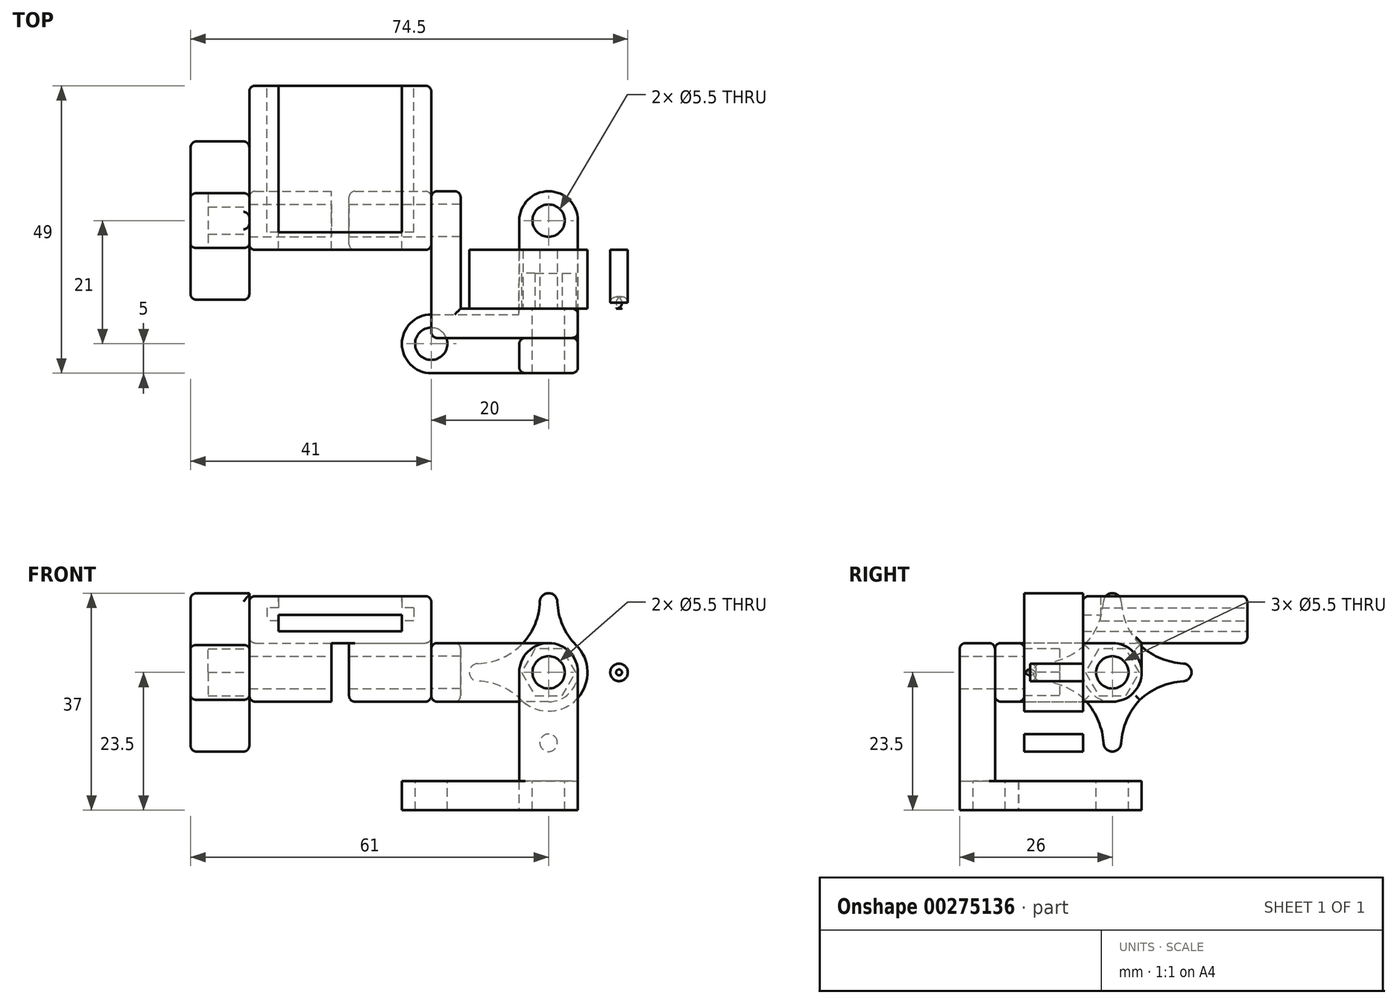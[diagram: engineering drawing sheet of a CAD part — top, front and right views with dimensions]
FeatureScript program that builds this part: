
annotation { "Feature Type Name" : "Feature", "Feature Type Description" : "" }
export const myFeature = defineFeature(function(context is Context, id is Id, definition is map)
    precondition{}
    {
        {
            var Q0;
            Q0=qCreatedBy(makeId("Top.planeOp"),FACE);
            var sketch = newSketch(context, id + "F0", { "sketchPlane" : qUnion([Q0])});
            skLineSegment(sketch, "E0.bottom", {"start": v(-15.5, 14) * mm, "end": v(15.5, 14) * mm});
            skLineSegment(sketch, "E0.top", {"start": v(-15.5, -14) * mm, "end": v(15.5, -14) * mm});
            skLineSegment(sketch, "E0.left", {"start": v(-15.5, 14) * mm, "end": v(-15.5, -14) * mm});
            skLineSegment(sketch, "E0.right", {"start": v(15.5, 14) * mm, "end": v(15.5, -14) * mm});
            skPoint(sketch, "E1", {"position": v(0, 14) * mm});
            skPoint(sketch, "E2", {"position": v(-15.5, 0) * mm});
            skSolve(sketch);
        }
        {
            var Q0;
            Q0=makeQuery(id+"F0.imprint","IMPRINT",FACE,{"disambiguationData":[TD([[makeQuery(id+"F0.imprint","IMPRINT",EDGE,{"derivedFrom":sQuery(id+"F0.wireOp",EDGE,"E0.bottom")}),-1.0]])]});
            extrude(context, id + "F1", {"entities" : qUnion([Q0]), "depth" : (4 + 4) * mm});
        }
        {
            var Q0;
            Q0=makeQuery(id+"F1.opExtrude","SWEPT_FACE",FACE,{"disambiguationData":[OSD([sQuery(id+"F0.wireOp",EDGE,"E0.bottom")])]});
            var sketch = newSketch(context, id + "F2", { "sketchPlane" : qUnion([Q0])});
            skLineSegment(sketch, "E3.bottom", {"start": v(-12.5, 6) * mm, "end": v(12.5, 6) * mm});
            skLineSegment(sketch, "E3.top", {"start": v(-12.5, 4.8) * mm, "end": v(12.5, 4.8) * mm});
            skLineSegment(sketch, "E3.left", {"start": v(-12.5, 6) * mm, "end": v(-12.5, 4.8) * mm});
            skLineSegment(sketch, "E3.right", {"start": v(12.5, 6) * mm, "end": v(12.5, 4.8) * mm});
            skLineSegment(sketch, "E4.bottom", {"start": v(-10.5, 8) * mm, "end": v(10.5, 8) * mm});
            skLineSegment(sketch, "E4.top", {"start": v(-10.5, 2) * mm, "end": v(10.5, 2) * mm});
            skLineSegment(sketch, "E4.left", {"start": v(-10.5, 8) * mm, "end": v(-10.5, 2) * mm});
            skLineSegment(sketch, "E4.right", {"start": v(10.5, 8) * mm, "end": v(10.5, 2) * mm});
            skSolve(sketch);
        }
        {
            var Q0;
            {var subQ5=sQuery(id+"F2.wireOp",EDGE,"E4.bottom");Q0=makeQuery(id+"F2.imprint","IMPRINT",FACE,{"disambiguationData":[TD([[makeQuery(id+"F2.imprint","IMPRINT",EDGE,{"derivedFrom":subQ5}),1.0]])]});}
            var Q1;
            {var subQ0=sQuery(id+"F2.wireOp",EDGE,"E4.left");var subQ1=sQuery(id+"F2.wireOp",EDGE,"E3.bottom");var subQ2=makeQuery(id+"F2.imprint","INTERSECT",VERTEX,{"derivedFrom":[subQ1,subQ0]});Q1=makeQuery(id+"F2.imprint","IMPRINT",FACE,{"disambiguationData":[TD([[makeQuery(id+"F2.imprint","IMPRINT",EDGE,{"disambiguationData":[TD([[subQ2,-1.0]])],"derivedFrom":subQ1}),-1.0]])]});}
            var Q2;
            {var subQ0=sQuery(id+"F2.wireOp",EDGE,"E3.left");Q2=makeQuery(id+"F2.imprint","IMPRINT",FACE,{"disambiguationData":[TD([[makeQuery(id+"F2.imprint","IMPRINT",EDGE,{"derivedFrom":subQ0}),1.0]])]});}
            var Q3;
            {var subQ5=sQuery(id+"F2.wireOp",EDGE,"E4.top");Q3=makeQuery(id+"F2.imprint","IMPRINT",FACE,{"disambiguationData":[TD([[makeQuery(id+"F2.imprint","IMPRINT",EDGE,{"derivedFrom":subQ5}),1.0]])]});}
            var Q4;
            {var subQ0=sQuery(id+"F2.wireOp",EDGE,"E3.right");Q4=makeQuery(id+"F2.imprint","IMPRINT",FACE,{"disambiguationData":[TD([[makeQuery(id+"F2.imprint","IMPRINT",EDGE,{"derivedFrom":subQ0}),-1.0]])]});}
            extrude(context, id + "F3", {"entities" : qUnion([Q0, Q1, Q2, Q3, Q4]), "operationType" : NewBodyOperationType.REMOVE, "oppositeDirection" : true, "depth" : 25 * mm});
        }
        {
            var Q0;
            Q0=makeQuery(id+"F3.boolean.opBoolean","COPY",FACE,{"derivedFrom":makeQuery(id+"F3.opExtrude","CAP_FACE",FACE,{"disambiguationData":[OSD([sQuery(id+"F2.wireOp",EDGE,"E3.bottom"),sQuery(id+"F2.wireOp",EDGE,"E3.top"),sQuery(id+"F2.wireOp",EDGE,"E3.left"),sQuery(id+"F2.wireOp",EDGE,"E3.right"),sQuery(id+"F2.wireOp",EDGE,"E4.bottom"),sQuery(id+"F2.wireOp",EDGE,"E4.top"),sQuery(id+"F2.wireOp",EDGE,"E4.left"),sQuery(id+"F2.wireOp",EDGE,"E4.right")])],"isStart":false})});
            var sketch = newSketch(context, id + "F4", { "sketchPlane" : qUnion([Q0])});
            skLineSegment(sketch, "E5.bottom", {"start": v(-10.5, 4.8) * mm, "end": v(10.5, 4.8) * mm});
            skLineSegment(sketch, "E5.top", {"start": v(-10.5, 2) * mm, "end": v(10.5, 2) * mm});
            skLineSegment(sketch, "E5.left", {"start": v(-10.5, 4.8) * mm, "end": v(-10.5, 2) * mm});
            skLineSegment(sketch, "E5.right", {"start": v(10.5, 4.8) * mm, "end": v(10.5, 2) * mm});
            skSolve(sketch);
        }
        {
            var Q0;
            Q0=makeQuery(id+"F4.imprint","IMPRINT",FACE,{"disambiguationData":[TD([[makeQuery(id+"F4.imprint","IMPRINT",EDGE,{"derivedFrom":sQuery(id+"F4.wireOp",EDGE,"E5.bottom")}),-1.0]])]});
            extrude(context, id + "F5", {"entities" : qUnion([Q0]), "operationType" : NewBodyOperationType.REMOVE, "endBound" : BoundingType.UP_TO_NEXT, "oppositeDirection" : true, "depth" : 25 * mm});
        }
        {
            var Q0;
            Q0=makeQuery(id+"F1.opExtrude","SWEPT_FACE",FACE,{"disambiguationData":[OSD([sQuery(id+"F0.wireOp",EDGE,"E0.right")])]});
            var sketch = newSketch(context, id + "F6", { "sketchPlane" : qUnion([Q0])});
            skLineSegment(sketch, "E6.bottom", {"start": v(-14, 0) * mm, "end": v(-4, 0) * mm});
            skLineSegment(sketch, "E6.top", {"start": v(-14, -10) * mm, "end": v(-4, -10) * mm});
            skLineSegment(sketch, "E6.left", {"start": v(-14, 0) * mm, "end": v(-14, -10) * mm});
            skLineSegment(sketch, "E6.right", {"start": v(-4, 0) * mm, "end": v(-4, -10) * mm});
            skCircle(sketch, "E7", {"center": v(-9, -5) * mm, "radius": 2.75 * mm});
            skPoint(sketch, "E8", {"position": v(-4, -5) * mm});
            skPoint(sketch, "E9", {"position": v(-9, -10) * mm});
            skCircle(sketch, "E10", {"center": v(-9, -5) * mm, "radius": 5 * mm});
            skSolve(sketch);
        }
        {
            var Q0;
            Q0=makeQuery(id+"F6.imprint","IMPRINT",FACE,{"disambiguationData":[TD([[makeQuery(id+"F6.imprint","IMPRINT",EDGE,{"derivedFrom":sQuery(id+"F6.wireOp",EDGE,"E7")}),-1.0]])]});
            var Q1;
            {var subQ0=sQuery(id+"F6.wireOp",EDGE,"E6.left");var subQ3=sQuery(id+"F6.wireOp",EDGE,"E10");var subQ5=makeQuery(id+"F6.imprint","INTERSECT",VERTEX,{"derivedFrom":[subQ0,subQ3]});Q1=makeQuery(id+"F6.imprint","IMPRINT",FACE,{"disambiguationData":[TD([[makeQuery(id+"F6.imprint","IMPRINT",EDGE,{"disambiguationData":[TD([[subQ5,1.0]])],"derivedFrom":subQ3}),-1.0]])]});}
            var Q2;
            {var subQ0=sQuery(id+"F6.wireOp",EDGE,"E6.right");var subQ3=sQuery(id+"F6.wireOp",EDGE,"E10");var subQ5=makeQuery(id+"F6.imprint","INTERSECT",VERTEX,{"derivedFrom":[subQ0,subQ3]});Q2=makeQuery(id+"F6.imprint","IMPRINT",FACE,{"disambiguationData":[TD([[makeQuery(id+"F6.imprint","IMPRINT",EDGE,{"disambiguationData":[TD([[subQ5,-1.0]])],"derivedFrom":subQ3}),-1.0]])]});}
            var Q3;
            Q3=makeQuery(id+"F1.opExtrude","SWEPT_FACE",FACE,{"disambiguationData":[OSD([sQuery(id+"F0.wireOp",EDGE,"E0.left")])]});
            extrude(context, id + "F7", {"entities" : qUnion([Q0, Q1, Q2]), "operationType" : NewBodyOperationType.ADD, "endBound" : BoundingType.UP_TO_SURFACE, "oppositeDirection" : true, "endBoundEntityFace" : qUnion([Q3]), "depth" : 25 * mm});
        }
        {
            var Q0;
            Q0=makeQuery(id+"F7.opExtrude","SWEPT_FACE",FACE,{"disambiguationData":[OSD([sQuery(id+"F6.wireOp",EDGE,"E6.right")])]});
            var sketch = newSketch(context, id + "F8", { "sketchPlane" : qUnion([Q0])});
            skLineSegment(sketch, "E11.bottom", {"start": v(-1.5, 0) * mm, "end": v(1.5, 0) * mm});
            skLineSegment(sketch, "E11.top", {"start": v(-1.5, -11.71) * mm, "end": v(1.5, -11.71) * mm});
            skLineSegment(sketch, "E11.left", {"start": v(-1.5, 0) * mm, "end": v(-1.5, -11.71) * mm});
            skLineSegment(sketch, "E11.right", {"start": v(1.5, 0) * mm, "end": v(1.5, -11.71) * mm});
            skPoint(sketch, "E12", {"position": v(0, 0) * mm});
            skSolve(sketch);
        }
        {
            var Q0;
            {var subQ0=sQuery(id+"F2.wireOp",EDGE,"E3.top");Q0=makeQuery(id+"F3.boolean.opBoolean","COPY",FACE,{"derivedFrom":makeQuery(id+"F3.opExtrude","SWEPT_FACE",FACE,{"disambiguationData":[OSD([subQ0]),TDD([makeQuery(id+"F2.imprint","IMPRINT",EDGE,{"disambiguationData":[TD([[makeQuery(id+"F2.imprint","INTERSECT",VERTEX,{"derivedFrom":[subQ0,sQuery(id+"F2.wireOp",EDGE,"E3.right")]}),1.0]])],"derivedFrom":subQ0})])]})});}
            var Q1;
            {var subQ0=sQuery(id+"F2.wireOp",EDGE,"E3.top");Q1=makeQuery(id+"F3.boolean.opBoolean","COPY",FACE,{"derivedFrom":makeQuery(id+"F3.opExtrude","SWEPT_FACE",FACE,{"disambiguationData":[OSD([subQ0]),TDD([makeQuery(id+"F2.imprint","IMPRINT",EDGE,{"disambiguationData":[TD([[makeQuery(id+"F2.imprint","INTERSECT",VERTEX,{"derivedFrom":[subQ0,sQuery(id+"F2.wireOp",EDGE,"E3.left")]}),-1.0]])],"derivedFrom":subQ0})])]})});}
            extrude(context, id + "F9", {"entities" : qUnion([Q0, Q1]), "operationType" : NewBodyOperationType.REMOVE, "oppositeDirection" : true, "depth" : 1 * mm});
        }
        {
            var Q0;
            {var subQ0=sQuery(id+"F8.wireOp",EDGE,"E11.bottom");Q0=makeQuery(id+"F8.imprint","IMPRINT",FACE,{"disambiguationData":[TD([[makeQuery(id+"F8.imprint","IMPRINT",EDGE,{"derivedFrom":subQ0}),1.0]])]});}
            var Q1;
            {var subQ0=sQuery(id+"F8.wireOp",EDGE,"E11.top");Q1=makeQuery(id+"F8.imprint","IMPRINT",FACE,{"disambiguationData":[TD([[makeQuery(id+"F8.imprint","IMPRINT",EDGE,{"derivedFrom":subQ0}),1.0]])]});}
            extrude(context, id + "F10", {"entities" : qUnion([Q0, Q1]), "operationType" : NewBodyOperationType.REMOVE, "endBound" : BoundingType.THROUGH_ALL, "oppositeDirection" : true, "depth" : 25 * mm});
        }
        {
            var Q0;
            Q0=makeQuery(id+"F1.opExtrude","CAP_EDGE",EDGE,{"disambiguationData":[OSD([sQuery(id+"F0.wireOp",EDGE,"E0.left")])],"isStart":false});
            var Q1;
            Q1=makeQuery(id+"F1.opExtrude","CAP_EDGE",EDGE,{"disambiguationData":[OSD([sQuery(id+"F0.wireOp",EDGE,"E0.left")])],"isStart":true});
            var Q2;
            Q2=makeQuery(id+"F1.opExtrude","CAP_EDGE",EDGE,{"disambiguationData":[OSD([sQuery(id+"F0.wireOp",EDGE,"E0.right")])],"isStart":true});
            var Q3;
            Q3=makeQuery(id+"F1.opExtrude","CAP_EDGE",EDGE,{"disambiguationData":[OSD([sQuery(id+"F0.wireOp",EDGE,"E0.right")])],"isStart":false});
            var Q4;
            Q4=makeQuery(id+"F3.boolean.opBoolean","COPY",EDGE,{"derivedFrom":makeQuery(id+"F3.opExtrude","SWEPT_EDGE",EDGE,{"disambiguationData":[OSD([sQuery(id+"F0.wireOp",EDGE,"E0.bottom"),sQuery(id+"F2.wireOp",EDGE,"E4.bottom"),sQuery(id+"F2.wireOp",EDGE,"E4.right")])]})});
            var Q5;
            Q5=makeQuery(id+"F3.boolean.opBoolean","COPY",EDGE,{"derivedFrom":makeQuery(id+"F3.opExtrude","SWEPT_EDGE",EDGE,{"disambiguationData":[OSD([sQuery(id+"F0.wireOp",EDGE,"E0.bottom"),sQuery(id+"F2.wireOp",EDGE,"E4.bottom"),sQuery(id+"F2.wireOp",EDGE,"E4.left")])]})});
            var Q6;
            Q6=makeQuery(id+"F3.boolean.opBoolean","COPY",EDGE,{"derivedFrom":makeQuery(id+"F3.opExtrude","CAP_EDGE",EDGE,{"disambiguationData":[OSD([sQuery(id+"F2.wireOp",EDGE,"E4.bottom")])],"isStart":false})});
            var Q7;
            Q7=makeQuery(id+"F5.boolean.opBoolean","COPY",EDGE,{"derivedFrom":makeQuery(id+"F5.opExtrude","CAP_EDGE",EDGE,{"disambiguationData":[OSD([sQuery(id+"F4.wireOp",EDGE,"E5.bottom")])],"isStart":true})});
            var Q8;
            Q8=makeQuery(id+"F1.opExtrude","CAP_EDGE",EDGE,{"disambiguationData":[OSD([sQuery(id+"F0.wireOp",EDGE,"E0.bottom")])],"isStart":true});
            var Q9;
            Q9=makeQuery(id+"F1.opExtrude","SWEPT_EDGE",EDGE,{"disambiguationData":[OSD([sQuery(id+"F0.wireOp",EDGE,"E0.bottom"),sQuery(id+"F0.wireOp",EDGE,"E0.left")])]});
            var Q10;
            Q10=makeQuery(id+"F1.opExtrude","SWEPT_EDGE",EDGE,{"disambiguationData":[OSD([sQuery(id+"F0.wireOp",EDGE,"E0.bottom"),sQuery(id+"F0.wireOp",EDGE,"E0.right")])]});
            var Q11;
            {var subQ0=sQuery(id+"F0.wireOp",EDGE,"E0.bottom");var subQ2=makeQuery(id+"F1.opExtrude","CAP_EDGE",EDGE,{"disambiguationData":[OSD([subQ0])],"isStart":false});var subQ3=sQuery(id+"F0.wireOp",EDGE,"E0.right");Q11=makeQuery(id+"F3.boolean.opBoolean","SPLIT",EDGE,{"disambiguationData":[TD([makeQuery(id+"F1.opExtrude","SWEPT_FACE",FACE,{"disambiguationData":[OSD([subQ3])]})])],"derivedFrom":subQ2});}
            var Q12;
            {var subQ0=sQuery(id+"F0.wireOp",EDGE,"E0.bottom");var subQ1=sQuery(id+"F0.wireOp",EDGE,"E0.left");var subQ3=makeQuery(id+"F1.opExtrude","CAP_EDGE",EDGE,{"disambiguationData":[OSD([subQ0])],"isStart":false});Q12=makeQuery(id+"F3.boolean.opBoolean","SPLIT",EDGE,{"disambiguationData":[TD([makeQuery(id+"F1.opExtrude","SWEPT_FACE",FACE,{"disambiguationData":[OSD([subQ1])]})])],"derivedFrom":subQ3});}
            var Q13;
            Q13=makeQuery(id+"F3.boolean.opBoolean","COPY",EDGE,{"derivedFrom":makeQuery(id+"F3.opExtrude","CAP_EDGE",EDGE,{"disambiguationData":[OSD([sQuery(id+"F2.wireOp",EDGE,"E4.top")])],"isStart":true})});
            var Q14;
            {var subQ0=sQuery(id+"F2.wireOp",EDGE,"E4.left");Q14=makeQuery(id+"F3.boolean.opBoolean","COPY",EDGE,{"derivedFrom":makeQuery(id+"F3.opExtrude","CAP_EDGE",EDGE,{"disambiguationData":[OSD([subQ0]),TDD([makeQuery(id+"F2.imprint","IMPRINT",EDGE,{"disambiguationData":[TD([[makeQuery(id+"F2.imprint","INTERSECT",VERTEX,{"derivedFrom":[sQuery(id+"F2.wireOp",EDGE,"E4.top"),subQ0]}),1.0]])],"derivedFrom":subQ0})])],"isStart":true})});}
            var Q15;
            {var subQ0=sQuery(id+"F2.wireOp",EDGE,"E4.right");Q15=makeQuery(id+"F3.boolean.opBoolean","COPY",EDGE,{"derivedFrom":makeQuery(id+"F3.opExtrude","CAP_EDGE",EDGE,{"disambiguationData":[OSD([subQ0]),TDD([makeQuery(id+"F2.imprint","IMPRINT",EDGE,{"disambiguationData":[TD([[makeQuery(id+"F2.imprint","INTERSECT",VERTEX,{"derivedFrom":[sQuery(id+"F2.wireOp",EDGE,"E4.top"),subQ0]}),1.0]])],"derivedFrom":subQ0})])],"isStart":true})});}
            var Q16;
            Q16=makeQuery(id+"F3.boolean.opBoolean","COPY",EDGE,{"derivedFrom":makeQuery(id+"F3.opExtrude","CAP_EDGE",EDGE,{"disambiguationData":[OSD([sQuery(id+"F2.wireOp",EDGE,"E3.left")])],"isStart":true})});
            var Q17;
            {var subQ0=sQuery(id+"F2.wireOp",EDGE,"E3.top");Q17=makeQuery(id+"F3.boolean.opBoolean","COPY",EDGE,{"derivedFrom":makeQuery(id+"F3.opExtrude","CAP_EDGE",EDGE,{"disambiguationData":[OSD([subQ0]),TDD([makeQuery(id+"F2.imprint","IMPRINT",EDGE,{"disambiguationData":[TD([[makeQuery(id+"F2.imprint","INTERSECT",VERTEX,{"derivedFrom":[subQ0,sQuery(id+"F2.wireOp",EDGE,"E3.left")]}),-1.0]])],"derivedFrom":subQ0})])],"isStart":true})});}
            var Q18;
            {var subQ0=sQuery(id+"F2.wireOp",EDGE,"E3.bottom");Q18=makeQuery(id+"F3.boolean.opBoolean","COPY",EDGE,{"derivedFrom":makeQuery(id+"F3.opExtrude","CAP_EDGE",EDGE,{"disambiguationData":[OSD([subQ0]),TDD([makeQuery(id+"F2.imprint","IMPRINT",EDGE,{"disambiguationData":[TD([[makeQuery(id+"F2.imprint","INTERSECT",VERTEX,{"derivedFrom":[subQ0,sQuery(id+"F2.wireOp",EDGE,"E3.left")]}),-1.0]])],"derivedFrom":subQ0})])],"isStart":true})});}
            var Q19;
            Q19=makeQuery(id+"F3.boolean.opBoolean","COPY",EDGE,{"derivedFrom":makeQuery(id+"F3.opExtrude","CAP_EDGE",EDGE,{"disambiguationData":[OSD([sQuery(id+"F2.wireOp",EDGE,"E3.right")])],"isStart":true})});
            var Q20;
            {var subQ0=sQuery(id+"F2.wireOp",EDGE,"E3.top");Q20=makeQuery(id+"F3.boolean.opBoolean","COPY",EDGE,{"derivedFrom":makeQuery(id+"F3.opExtrude","CAP_EDGE",EDGE,{"disambiguationData":[OSD([subQ0]),TDD([makeQuery(id+"F2.imprint","IMPRINT",EDGE,{"disambiguationData":[TD([[makeQuery(id+"F2.imprint","INTERSECT",VERTEX,{"derivedFrom":[subQ0,sQuery(id+"F2.wireOp",EDGE,"E3.right")]}),1.0]])],"derivedFrom":subQ0})])],"isStart":true})});}
            var Q21;
            {var subQ0=sQuery(id+"F2.wireOp",EDGE,"E3.bottom");Q21=makeQuery(id+"F3.boolean.opBoolean","COPY",EDGE,{"derivedFrom":makeQuery(id+"F3.opExtrude","CAP_EDGE",EDGE,{"disambiguationData":[OSD([subQ0]),TDD([makeQuery(id+"F2.imprint","IMPRINT",EDGE,{"disambiguationData":[TD([[makeQuery(id+"F2.imprint","INTERSECT",VERTEX,{"derivedFrom":[subQ0,sQuery(id+"F2.wireOp",EDGE,"E3.right")]}),1.0]])],"derivedFrom":subQ0})])],"isStart":true})});}
            var Q22;
            {var subQ0=sQuery(id+"F2.wireOp",EDGE,"E4.right");Q22=makeQuery(id+"F3.boolean.opBoolean","COPY",EDGE,{"derivedFrom":makeQuery(id+"F3.opExtrude","CAP_EDGE",EDGE,{"disambiguationData":[OSD([subQ0]),TDD([makeQuery(id+"F2.imprint","IMPRINT",EDGE,{"disambiguationData":[TD([[makeQuery(id+"F2.imprint","INTERSECT",VERTEX,{"derivedFrom":[sQuery(id+"F2.wireOp",EDGE,"E3.bottom"),subQ0]}),1.0]])],"derivedFrom":subQ0})])],"isStart":true})});}
            var Q23;
            {var subQ0=sQuery(id+"F2.wireOp",EDGE,"E4.left");Q23=makeQuery(id+"F3.boolean.opBoolean","COPY",EDGE,{"derivedFrom":makeQuery(id+"F3.opExtrude","CAP_EDGE",EDGE,{"disambiguationData":[OSD([subQ0]),TDD([makeQuery(id+"F2.imprint","IMPRINT",EDGE,{"disambiguationData":[TD([[makeQuery(id+"F2.imprint","INTERSECT",VERTEX,{"derivedFrom":[sQuery(id+"F2.wireOp",EDGE,"E3.bottom"),subQ0]}),1.0]])],"derivedFrom":subQ0})])],"isStart":true})});}
            var Q24;
            Q24=makeQuery(id+"F5.boolean.opBoolean","COPY",EDGE,{"derivedFrom":makeQuery(id+"F5.opExtrude","TWEAK_EDGE",EDGE,{"derivedFrom":[makeQuery(id+"F1.opExtrude","SWEPT_FACE",FACE,{"disambiguationData":[OSD([sQuery(id+"F0.wireOp",EDGE,"E0.top")])]}),makeQuery(id+"F4.imprint","IMPRINT",EDGE,{"derivedFrom":sQuery(id+"F4.wireOp",EDGE,"E5.top")})]})});
            var Q25;
            Q25=makeQuery(id+"F5.boolean.opBoolean","COPY",EDGE,{"derivedFrom":makeQuery(id+"F5.opExtrude","TWEAK_EDGE",EDGE,{"derivedFrom":[makeQuery(id+"F1.opExtrude","SWEPT_FACE",FACE,{"disambiguationData":[OSD([sQuery(id+"F0.wireOp",EDGE,"E0.top")])]}),makeQuery(id+"F4.imprint","IMPRINT",EDGE,{"derivedFrom":sQuery(id+"F4.wireOp",EDGE,"E5.bottom")})]})});
            var Q26;
            Q26=makeQuery(id+"F5.boolean.opBoolean","COPY",EDGE,{"derivedFrom":makeQuery(id+"F5.opExtrude","TWEAK_EDGE",EDGE,{"derivedFrom":[makeQuery(id+"F1.opExtrude","SWEPT_FACE",FACE,{"disambiguationData":[OSD([sQuery(id+"F0.wireOp",EDGE,"E0.top")])]}),makeQuery(id+"F4.imprint","IMPRINT",EDGE,{"derivedFrom":sQuery(id+"F4.wireOp",EDGE,"E5.left")})]})});
            var Q27;
            Q27=makeQuery(id+"F5.boolean.opBoolean","COPY",EDGE,{"derivedFrom":makeQuery(id+"F5.opExtrude","TWEAK_EDGE",EDGE,{"derivedFrom":[makeQuery(id+"F1.opExtrude","SWEPT_FACE",FACE,{"disambiguationData":[OSD([sQuery(id+"F0.wireOp",EDGE,"E0.top")])]}),makeQuery(id+"F4.imprint","IMPRINT",EDGE,{"derivedFrom":sQuery(id+"F4.wireOp",EDGE,"E5.right")})]})});
            var Q28;
            Q28=makeQuery(id+"F1.opExtrude","CAP_EDGE",EDGE,{"disambiguationData":[OSD([sQuery(id+"F0.wireOp",EDGE,"E0.top")])],"isStart":false});
            var Q29;
            Q29=makeQuery(id+"F1.opExtrude","SWEPT_EDGE",EDGE,{"disambiguationData":[OSD([sQuery(id+"F0.wireOp",EDGE,"E0.top"),sQuery(id+"F0.wireOp",EDGE,"E0.right")])]});
            var Q30;
            Q30=makeQuery(id+"F1.opExtrude","CAP_EDGE",EDGE,{"disambiguationData":[OSD([sQuery(id+"F0.wireOp",EDGE,"E0.top")])],"isStart":true});
            var Q31;
            Q31=makeQuery(id+"F1.opExtrude","SWEPT_EDGE",EDGE,{"disambiguationData":[OSD([sQuery(id+"F0.wireOp",EDGE,"E0.top"),sQuery(id+"F0.wireOp",EDGE,"E0.left")])]});
            var Q32;
            Q32=makeQuery(id+"F10.boolean.opBoolean","COPY",EDGE,{"derivedFrom":makeQuery(id+"F10.opExtrude","CAP_EDGE",EDGE,{"disambiguationData":[OSD([sQuery(id+"F8.wireOp",EDGE,"E11.left")])],"isStart":true})});
            var Q33;
            Q33=makeQuery(id+"F10.boolean.opBoolean","COPY",EDGE,{"derivedFrom":makeQuery(id+"F10.opExtrude","CAP_EDGE",EDGE,{"disambiguationData":[OSD([sQuery(id+"F8.wireOp",EDGE,"E11.right")])],"isStart":true})});
            var Q34;
            {var subQ0=sQuery(id+"F2.wireOp",EDGE,"E3.top");Q34=makeQuery(id+"F9.boolean.opBoolean","COPY",EDGE,{"derivedFrom":makeQuery(id+"F9.opExtrude","CAP_EDGE",EDGE,{"disambiguationData":[OSD([subQ0]),TDD([makeQuery(id+"F3.boolean.opBoolean","COPY",EDGE,{"derivedFrom":makeQuery(id+"F3.opExtrude","CAP_EDGE",EDGE,{"disambiguationData":[OSD([subQ0]),TDD([makeQuery(id+"F2.imprint","IMPRINT",EDGE,{"disambiguationData":[TD([[makeQuery(id+"F2.imprint","INTERSECT",VERTEX,{"derivedFrom":[subQ0,sQuery(id+"F2.wireOp",EDGE,"E3.right")]}),1.0]])],"derivedFrom":subQ0})])],"isStart":true})})])],"isStart":false})});}
            var Q35;
            {var subQ0=sQuery(id+"F2.wireOp",EDGE,"E3.top");Q35=makeQuery(id+"F9.boolean.opBoolean","COPY",EDGE,{"derivedFrom":makeQuery(id+"F9.opExtrude","CAP_EDGE",EDGE,{"disambiguationData":[OSD([subQ0]),TDD([makeQuery(id+"F3.boolean.opBoolean","COPY",EDGE,{"derivedFrom":makeQuery(id+"F3.opExtrude","CAP_EDGE",EDGE,{"disambiguationData":[OSD([subQ0]),TDD([makeQuery(id+"F2.imprint","IMPRINT",EDGE,{"disambiguationData":[TD([[makeQuery(id+"F2.imprint","INTERSECT",VERTEX,{"derivedFrom":[subQ0,sQuery(id+"F2.wireOp",EDGE,"E3.left")]}),-1.0]])],"derivedFrom":subQ0})])],"isStart":true})})])],"isStart":false})});}
            fillet(context, id + "F11", {"entities" : qUnion([Q0, Q1, Q2, Q3, Q4, Q5, Q6, Q7, Q8, Q9, Q10, Q11, Q12, Q13, Q14, Q15, Q16, Q17, Q18, Q19, Q20, Q21, Q22, Q23, Q24, Q25, Q26, Q27, Q28, Q29, Q30, Q31, Q32, Q33, Q34, Q35]), "radius" : 1 * mm, "tangentPropagation" : true, "allowEdgeOverflow" : false});
        }
        {
            var Q0;
            {var subQ0=sQuery(id+"F0.wireOp",EDGE,"E0.left");Q0=makeQuery(id+"F7.boolean.opBoolean","MERGE",FACE,{"derivedFrom":[makeQuery(id+"F1.opExtrude","SWEPT_FACE",FACE,{"disambiguationData":[OSD([subQ0])]}),makeQuery(id+"F7.opExtrude","CAP_FACE",FACE,{"disambiguationData":[OSD([subQ0])],"isStart":false})]});}
            var sketch = newSketch(context, id + "F12", { "sketchPlane" : qUnion([Q0])});
            skCircle(sketch, "E13.cCircle", {"center": v(9, -5) * mm, "radius": 4 * mm, "construction": true});
            skLineSegment(sketch, "E13.0", {"start": v(6.7, -1) * mm, "end": v(11.3, -1) * mm});
            skLineSegment(sketch, "E13.1", {"start": v(11.3, -1) * mm, "end": v(13.62, -5) * mm});
            skLineSegment(sketch, "E13.2", {"start": v(13.62, -5) * mm, "end": v(11.3, -9) * mm});
            skLineSegment(sketch, "E13.3", {"start": v(11.3, -9) * mm, "end": v(6.7, -9) * mm});
            skLineSegment(sketch, "E13.4", {"start": v(6.7, -9) * mm, "end": v(4.38, -5) * mm});
            skLineSegment(sketch, "E13.5", {"start": v(4.38, -5) * mm, "end": v(6.7, -1) * mm});
            skPoint(sketch, "E13.0.midPoint", {"position": v(9, -1) * mm});
            skCircle(sketch, "E14", {"center": v(9, -5) * mm, "radius": 6.62 * mm});
            skCircle(sketch, "E15", {"center": v(9, 7) * mm, "radius": 1.5 * mm});
            skLineSegment(sketch, "E16", {"start": v(9, -5) * mm, "end": v(4.32, -0.32) * mm});
            skLineSegment(sketch, "E17", {"start": v(9, -5) * mm, "end": v(13.68, -0.32) * mm});
            skArc(sketch, "E18", {"start": v(4.32, -0.32) * mm, "mid": v(6.55, 3.11) * mm, "end": v(7.5, 7.1) * mm});
            skArc(sketch, "E19", {"start": v(10.5, 7.1) * mm, "mid": v(11.45, 3.11) * mm, "end": v(13.68, -0.32) * mm});
            skArc(sketch, "E20.1.0", {"start": v(-3.1, -3.5) * mm, "mid": v(0.89, -2.55) * mm, "end": v(4.32, -0.32) * mm});
            skArc(sketch, "E20.1.1", {"start": v(4.32, -9.68) * mm, "mid": v(0.89, -7.45) * mm, "end": v(-3.1, -6.5) * mm});
            skCircle(sketch, "E20.1.2", {"center": v(-3, -5) * mm, "radius": 1.5 * mm});
            skArc(sketch, "E20.2.0", {"start": v(7.5, -17.1) * mm, "mid": v(6.55, -13.11) * mm, "end": v(4.32, -9.68) * mm});
            skArc(sketch, "E20.2.1", {"start": v(13.68, -9.68) * mm, "mid": v(11.45, -13.11) * mm, "end": v(10.5, -17.1) * mm});
            skCircle(sketch, "E20.2.2", {"center": v(9, -17) * mm, "radius": 1.5 * mm});
            skArc(sketch, "E20.3.0", {"start": v(21.1, -6.5) * mm, "mid": v(17.11, -7.45) * mm, "end": v(13.68, -9.68) * mm});
            skArc(sketch, "E20.3.1", {"start": v(13.68, -0.32) * mm, "mid": v(17.11, -2.55) * mm, "end": v(21.1, -3.5) * mm});
            skCircle(sketch, "E20.3.2", {"center": v(21, -5) * mm, "radius": 1.5 * mm});
            skSolve(sketch);
        }
        {
            var Q0;
            {var subQ1=sQuery(id+"F0.wireOp",EDGE,"E0.left");var subQ2=makeQuery(id+"F1.opExtrude","SWEPT_FACE",FACE,{"disambiguationData":[OSD([subQ1])]});var subQ3=makeQuery(id+"F7.boolean.opBoolean","MERGE",FACE,{"derivedFrom":[subQ2,makeQuery(id+"F7.opExtrude","CAP_FACE",FACE,{"disambiguationData":[OSD([subQ1])],"isStart":false})]});var subQ4=makeQuery(id+"F11.opFillet","BLEND_EDGE",EDGE,{"blendedFrom":[makeQuery(id+"F1.opExtrude","CAP_EDGE",EDGE,{"disambiguationData":[OSD([subQ1])],"isStart":false}),subQ3],"blendedInto":[subQ3]});var subQ18=sQuery(id+"F12.wireOp",EDGE,"E15");var subQ19=makeQuery(id+"F12.imprint","INTERSECT",VERTEX,{"disambiguationData":[OD(0.0)],"derivedFrom":[subQ4,subQ18]});Q0=makeQuery(id+"F12.imprint","IMPRINT",FACE,{"disambiguationData":[TD([[makeQuery(id+"F12.imprint","IMPRINT",EDGE,{"disambiguationData":[TD([[subQ19,-1.0]])],"derivedFrom":subQ18}),-1.0]])]});}
            var Q1;
            {var subQ0=sQuery(id+"F12.wireOp",EDGE,"E15");var subQ1=sQuery(id+"F0.wireOp",EDGE,"E0.left");var subQ2=makeQuery(id+"F11.opFillet","BLEND_EDGE",EDGE,{"blendedFrom":[makeQuery(id+"F1.opExtrude","CAP_EDGE",EDGE,{"disambiguationData":[OSD([subQ1])],"isStart":false}),makeQuery(id+"F7.boolean.opBoolean","MERGE",FACE,{"derivedFrom":[makeQuery(id+"F1.opExtrude","SWEPT_FACE",FACE,{"disambiguationData":[OSD([subQ1])]}),makeQuery(id+"F7.opExtrude","CAP_FACE",FACE,{"disambiguationData":[OSD([subQ1])],"isStart":false})]})],"blendedInto":[makeQuery(id+"F7.boolean.opBoolean","MERGE",FACE,{"derivedFrom":[makeQuery(id+"F1.opExtrude","SWEPT_FACE",FACE,{"disambiguationData":[OSD([subQ1])]}),makeQuery(id+"F7.opExtrude","CAP_FACE",FACE,{"disambiguationData":[OSD([subQ1])],"isStart":false})]})]});var subQ3=makeQuery(id+"F12.imprint","INTERSECT",VERTEX,{"disambiguationData":[OD(0.0)],"derivedFrom":[subQ2,subQ0]});Q1=makeQuery(id+"F12.imprint","IMPRINT",FACE,{"disambiguationData":[TD([[makeQuery(id+"F12.imprint","IMPRINT",EDGE,{"disambiguationData":[TD([[subQ3,-1.0]])],"derivedFrom":subQ0}),1.0]])]});}
            var Q2;
            {var subQ0=sQuery(id+"F12.wireOp",EDGE,"E15");var subQ1=makeQuery(id+"F12.imprint","INTERSECT",VERTEX,{"derivedFrom":[subQ0,sQuery(id+"F12.wireOp",EDGE,"E18")]});Q2=makeQuery(id+"F12.imprint","IMPRINT",FACE,{"disambiguationData":[TD([[makeQuery(id+"F12.imprint","IMPRINT",EDGE,{"disambiguationData":[TD([[subQ1,1.0]])],"derivedFrom":subQ0}),1.0]])]});}
            var Q3;
            {var subQ0=sQuery(id+"F12.wireOp",EDGE,"E20.1.2");var subQ1=makeQuery(id+"F12.imprint","INTERSECT",VERTEX,{"derivedFrom":[sQuery(id+"F12.wireOp",EDGE,"E20.1.0"),subQ0]});Q3=makeQuery(id+"F12.imprint","IMPRINT",FACE,{"disambiguationData":[TD([[makeQuery(id+"F12.imprint","IMPRINT",EDGE,{"disambiguationData":[TD([[subQ1,-1.0]])],"derivedFrom":subQ0}),1.0]])]});}
            var Q4;
            {var subQ0=sQuery(id+"F12.wireOp",EDGE,"E20.1.0");Q4=makeQuery(id+"F12.imprint","IMPRINT",FACE,{"disambiguationData":[TD([[makeQuery(id+"F12.imprint","IMPRINT",EDGE,{"derivedFrom":subQ0}),-1.0]])]});}
            var Q5;
            {var subQ0=sQuery(id+"F12.wireOp",EDGE,"E20.2.0");Q5=makeQuery(id+"F12.imprint","IMPRINT",FACE,{"disambiguationData":[TD([[makeQuery(id+"F12.imprint","IMPRINT",EDGE,{"derivedFrom":subQ0}),-1.0]])]});}
            var Q6;
            {var subQ0=sQuery(id+"F12.wireOp",EDGE,"E20.2.2");var subQ1=makeQuery(id+"F12.imprint","INTERSECT",VERTEX,{"derivedFrom":[sQuery(id+"F12.wireOp",EDGE,"E20.2.0"),subQ0]});Q6=makeQuery(id+"F12.imprint","IMPRINT",FACE,{"disambiguationData":[TD([[makeQuery(id+"F12.imprint","IMPRINT",EDGE,{"disambiguationData":[TD([[subQ1,-1.0]])],"derivedFrom":subQ0}),1.0]])]});}
            var Q7;
            {var subQ2=sQuery(id+"F12.wireOp",EDGE,"E20.3.0");Q7=makeQuery(id+"F12.imprint","IMPRINT",FACE,{"disambiguationData":[TD([[makeQuery(id+"F12.imprint","IMPRINT",EDGE,{"derivedFrom":subQ2}),-1.0]])]});}
            var Q8;
            {var subQ0=sQuery(id+"F12.wireOp",EDGE,"E20.3.2");var subQ1=makeQuery(id+"F12.imprint","INTERSECT",VERTEX,{"derivedFrom":[sQuery(id+"F12.wireOp",EDGE,"E20.3.0"),subQ0]});Q8=makeQuery(id+"F12.imprint","IMPRINT",FACE,{"disambiguationData":[TD([[makeQuery(id+"F12.imprint","IMPRINT",EDGE,{"disambiguationData":[TD([[subQ1,-1.0]])],"derivedFrom":subQ0}),1.0]])]});}
            var Q9;
            {var subQ0=sQuery(id+"F12.wireOp",EDGE,"E14");var subQ1=makeQuery(id+"F12.imprint","INTERSECT",VERTEX,{"derivedFrom":[subQ0,sQuery(id+"F12.wireOp",EDGE,"E20.1.1"),sQuery(id+"F12.wireOp",EDGE,"E20.2.0")]});Q9=makeQuery(id+"F12.imprint","IMPRINT",FACE,{"disambiguationData":[TD([[makeQuery(id+"F12.imprint","IMPRINT",EDGE,{"disambiguationData":[TD([[subQ1,-1.0]])],"derivedFrom":subQ0}),1.0]])]});}
            var Q10;
            {var subQ19=sQuery(id+"F12.wireOp",EDGE,"E13.0");Q10=makeQuery(id+"F12.imprint","IMPRINT",FACE,{"disambiguationData":[TD([[makeQuery(id+"F12.imprint","IMPRINT",EDGE,{"derivedFrom":subQ19}),1.0]])]});}
            var Q11;
            {var subQ0=sQuery(id+"F12.wireOp",EDGE,"E18");var subQ1=sQuery(id+"F12.wireOp",EDGE,"E14");var subQ2=makeQuery(id+"F12.imprint","INTERSECT",VERTEX,{"derivedFrom":[subQ1,sQuery(id+"F12.wireOp",EDGE,"E16"),subQ0,sQuery(id+"F12.wireOp",EDGE,"E20.1.0")]});Q11=makeQuery(id+"F12.imprint","IMPRINT",FACE,{"disambiguationData":[TD([[makeQuery(id+"F12.imprint","IMPRINT",EDGE,{"disambiguationData":[TD([[subQ2,1.0]])],"derivedFrom":subQ1}),-1.0]])]});}
            var Q12;
            {var subQ0=sQuery(id+"F12.wireOp",EDGE,"E16");var subQ1=sQuery(id+"F12.wireOp",EDGE,"E13.5");var subQ2=makeQuery(id+"F12.imprint","INTERSECT",VERTEX,{"derivedFrom":[subQ1,subQ0]});Q12=makeQuery(id+"F12.imprint","IMPRINT",FACE,{"disambiguationData":[TD([[makeQuery(id+"F12.imprint","IMPRINT",EDGE,{"disambiguationData":[TD([[subQ2,1.0]])],"derivedFrom":subQ1}),1.0]])]});}
            var Q13;
            {var subQ0=sQuery(id+"F12.wireOp",EDGE,"E16");var subQ1=sQuery(id+"F12.wireOp",EDGE,"E14");var subQ2=makeQuery(id+"F12.imprint","INTERSECT",VERTEX,{"derivedFrom":[subQ1,subQ0,sQuery(id+"F12.wireOp",EDGE,"E18"),sQuery(id+"F12.wireOp",EDGE,"E20.1.0")]});Q13=makeQuery(id+"F12.imprint","IMPRINT",FACE,{"disambiguationData":[TD([[makeQuery(id+"F12.imprint","IMPRINT",EDGE,{"disambiguationData":[TD([[subQ2,1.0]])],"derivedFrom":subQ1}),1.0]])]});}
            var Q14;
            {var subQ0=sQuery(id+"F12.wireOp",EDGE,"E17");var subQ1=sQuery(id+"F12.wireOp",EDGE,"E13.1");var subQ2=makeQuery(id+"F12.imprint","INTERSECT",VERTEX,{"derivedFrom":[subQ1,subQ0]});Q14=makeQuery(id+"F12.imprint","IMPRINT",FACE,{"disambiguationData":[TD([[makeQuery(id+"F12.imprint","IMPRINT",EDGE,{"disambiguationData":[TD([[subQ2,-1.0]])],"derivedFrom":subQ1}),1.0]])]});}
            var Q15;
            {var subQ0=sQuery(id+"F12.wireOp",EDGE,"E17");var subQ1=sQuery(id+"F12.wireOp",EDGE,"E14");var subQ2=makeQuery(id+"F12.imprint","INTERSECT",VERTEX,{"derivedFrom":[subQ1,subQ0,sQuery(id+"F12.wireOp",EDGE,"E19"),sQuery(id+"F12.wireOp",EDGE,"E20.3.1")]});Q15=makeQuery(id+"F12.imprint","IMPRINT",FACE,{"disambiguationData":[TD([[makeQuery(id+"F12.imprint","IMPRINT",EDGE,{"disambiguationData":[TD([[subQ2,-1.0]])],"derivedFrom":subQ1}),1.0]])]});}
            var Q16;
            {var subQ0=sQuery(id+"F12.wireOp",EDGE,"E19");var subQ1=sQuery(id+"F12.wireOp",EDGE,"E14");var subQ2=makeQuery(id+"F12.imprint","INTERSECT",VERTEX,{"derivedFrom":[subQ1,sQuery(id+"F12.wireOp",EDGE,"E17"),subQ0,sQuery(id+"F12.wireOp",EDGE,"E20.3.1")]});Q16=makeQuery(id+"F12.imprint","IMPRINT",FACE,{"disambiguationData":[TD([[makeQuery(id+"F12.imprint","IMPRINT",EDGE,{"disambiguationData":[TD([[subQ2,-1.0]])],"derivedFrom":subQ1}),-1.0]])]});}
            var Q17;
            {var subQ0=sQuery(id+"F12.wireOp",EDGE,"E18");var subQ1=sQuery(id+"F12.wireOp",EDGE,"E15");var subQ2=makeQuery(id+"F12.imprint","INTERSECT",VERTEX,{"derivedFrom":[subQ1,subQ0]});Q17=makeQuery(id+"F12.imprint","IMPRINT",FACE,{"disambiguationData":[TD([[makeQuery(id+"F12.imprint","IMPRINT",EDGE,{"disambiguationData":[TD([[subQ2,-1.0]])],"derivedFrom":subQ1}),-1.0]])]});}
            var Q18;
            {var subQ0=sQuery(id+"F12.wireOp",EDGE,"E19");var subQ1=sQuery(id+"F12.wireOp",EDGE,"E15");var subQ2=makeQuery(id+"F12.imprint","INTERSECT",VERTEX,{"derivedFrom":[subQ1,subQ0]});Q18=makeQuery(id+"F12.imprint","IMPRINT",FACE,{"disambiguationData":[TD([[makeQuery(id+"F12.imprint","IMPRINT",EDGE,{"disambiguationData":[TD([[subQ2,1.0]])],"derivedFrom":subQ1}),-1.0]])]});}
            var Q19;
            {var subQ1=sQuery(id+"F0.wireOp",EDGE,"E0.left");var subQ2=makeQuery(id+"F1.opExtrude","SWEPT_FACE",FACE,{"disambiguationData":[OSD([subQ1])]});var subQ3=makeQuery(id+"F7.boolean.opBoolean","MERGE",FACE,{"derivedFrom":[subQ2,makeQuery(id+"F7.opExtrude","CAP_FACE",FACE,{"disambiguationData":[OSD([subQ1])],"isStart":false})]});var subQ4=makeQuery(id+"F11.opFillet","BLEND_EDGE",EDGE,{"blendedFrom":[makeQuery(id+"F1.opExtrude","CAP_EDGE",EDGE,{"disambiguationData":[OSD([subQ1])],"isStart":false}),subQ3],"blendedInto":[subQ3]});var subQ18=sQuery(id+"F12.wireOp",EDGE,"E15");var subQ20=makeQuery(id+"F12.imprint","INTERSECT",VERTEX,{"disambiguationData":[OD(0.0)],"derivedFrom":[subQ4,subQ18]});Q19=makeQuery(id+"F12.imprint","IMPRINT",FACE,{"disambiguationData":[TD([[makeQuery(id+"F12.imprint","IMPRINT",EDGE,{"disambiguationData":[TD([[subQ20,1.0]])],"derivedFrom":subQ18}),-1.0]])]});}
            var Q20;
            {var subQ0=sQuery(id+"F12.wireOp",EDGE,"E15");var subQ1=sQuery(id+"F0.wireOp",EDGE,"E0.left");var subQ2=makeQuery(id+"F11.opFillet","BLEND_EDGE",EDGE,{"blendedFrom":[makeQuery(id+"F1.opExtrude","CAP_EDGE",EDGE,{"disambiguationData":[OSD([subQ1])],"isStart":false}),makeQuery(id+"F7.boolean.opBoolean","MERGE",FACE,{"derivedFrom":[makeQuery(id+"F1.opExtrude","SWEPT_FACE",FACE,{"disambiguationData":[OSD([subQ1])]}),makeQuery(id+"F7.opExtrude","CAP_FACE",FACE,{"disambiguationData":[OSD([subQ1])],"isStart":false})]})],"blendedInto":[makeQuery(id+"F7.boolean.opBoolean","MERGE",FACE,{"derivedFrom":[makeQuery(id+"F1.opExtrude","SWEPT_FACE",FACE,{"disambiguationData":[OSD([subQ1])]}),makeQuery(id+"F7.opExtrude","CAP_FACE",FACE,{"disambiguationData":[OSD([subQ1])],"isStart":false})]})]});var subQ3=makeQuery(id+"F12.imprint","INTERSECT",VERTEX,{"disambiguationData":[OD(0.0)],"derivedFrom":[subQ2,subQ0]});Q20=makeQuery(id+"F12.imprint","IMPRINT",FACE,{"disambiguationData":[TD([[makeQuery(id+"F12.imprint","IMPRINT",EDGE,{"disambiguationData":[TD([[subQ3,1.0]])],"derivedFrom":subQ0}),1.0]])]});}
            extrude(context, id + "F13", {"entities" : qUnion([Q0, Q1, Q2, Q3, Q4, Q5, Q6, Q7, Q8, Q9, Q10, Q11, Q12, Q13, Q14, Q15, Q16, Q17, Q18, Q19, Q20]), "depth" : 10 * mm});
        }
        {
            var Q0;
            Q0=makeQuery(id+"F13.opExtrude","CAP_FACE",FACE,{"disambiguationData":[OSD([sQuery(id+"F0.wireOp",EDGE,"E0.left"),sQuery(id+"F12.wireOp",EDGE,"E13.0"),sQuery(id+"F12.wireOp",EDGE,"E13.1"),sQuery(id+"F12.wireOp",EDGE,"E13.2"),sQuery(id+"F12.wireOp",EDGE,"E13.3"),sQuery(id+"F12.wireOp",EDGE,"E13.4"),sQuery(id+"F12.wireOp",EDGE,"E13.5"),sQuery(id+"F12.wireOp",EDGE,"E15"),sQuery(id+"F12.wireOp",EDGE,"E18"),sQuery(id+"F12.wireOp",EDGE,"E19"),sQuery(id+"F12.wireOp",EDGE,"E20.1.0"),sQuery(id+"F12.wireOp",EDGE,"E20.1.1"),sQuery(id+"F12.wireOp",EDGE,"E20.1.2"),sQuery(id+"F12.wireOp",EDGE,"E20.2.0"),sQuery(id+"F12.wireOp",EDGE,"E20.2.1"),sQuery(id+"F12.wireOp",EDGE,"E20.2.2"),sQuery(id+"F12.wireOp",EDGE,"E20.3.0"),sQuery(id+"F12.wireOp",EDGE,"E20.3.1"),sQuery(id+"F12.wireOp",EDGE,"E20.3.2")])],"isStart":false});
            var sketch = newSketch(context, id + "F14", { "sketchPlane" : qUnion([Q0])});
            skCircle(sketch, "E21", {"center": v(9, -5) * mm, "radius": 2.75 * mm});
            skSolve(sketch);
        }
        {
            var Q0;
            Q0=makeQuery(id+"F14.imprint","IMPRINT",FACE,{"disambiguationData":[TD([[makeQuery(id+"F14.imprint","IMPRINT",EDGE,{"derivedFrom":makeQuery(id+"F13.opExtrude","CAP_EDGE",EDGE,{"disambiguationData":[OSD([sQuery(id+"F12.wireOp",EDGE,"E13.0")])],"isStart":false})}),-1.0]])]});
            var Q1;
            Q1=makeQuery(id+"F14.imprint","IMPRINT",FACE,{"disambiguationData":[TD([[makeQuery(id+"F14.imprint","IMPRINT",EDGE,{"derivedFrom":sQuery(id+"F14.wireOp",EDGE,"E21")}),1.0]])]});
            extrude(context, id + "F15", {"entities" : qUnion([Q0, Q1]), "operationType" : NewBodyOperationType.ADD, "oppositeDirection" : true, "depth" : 3 * mm});
        }
        {
            var Q0;
            Q0=makeQuery(id+"F7.boolean.opBoolean","MERGE",FACE,{"derivedFrom":[makeQuery(id+"F1.opExtrude","SWEPT_FACE",FACE,{"disambiguationData":[OSD([sQuery(id+"F0.wireOp",EDGE,"E0.right")])]}),makeQuery(id+"F7.opExtrude","CAP_FACE",FACE,{"disambiguationData":[OSD([sQuery(id+"F6.wireOp",EDGE,"E6.bottom"),sQuery(id+"F6.wireOp",EDGE,"E6.left"),sQuery(id+"F6.wireOp",EDGE,"E6.right"),sQuery(id+"F6.wireOp",EDGE,"E7"),sQuery(id+"F6.wireOp",EDGE,"E10")])],"isStart":true})]});
            var sketch = newSketch(context, id + "F16", { "sketchPlane" : qUnion([Q0])});
            skCircle(sketch, "E22", {"center": v(-9, -5) * mm, "radius": 5 * mm});
            skCircle(sketch, "E23", {"center": v(-9, -5) * mm, "radius": 2.75 * mm});
            skLineSegment(sketch, "E24", {"start": v(-9, 0) * mm, "end": v(-24, 0) * mm});
            skLineSegment(sketch, "E25", {"start": v(-24, 0) * mm, "end": v(-24, -10) * mm});
            skLineSegment(sketch, "E26", {"start": v(-24, -10) * mm, "end": v(-9, -10) * mm});
            skSolve(sketch);
        }
        {
            var Q0;
            {var subQ1=sQuery(id+"F16.wireOp",EDGE,"E25");Q0=makeQuery(id+"F16.imprint","IMPRINT",FACE,{"disambiguationData":[TD([[makeQuery(id+"F16.imprint","IMPRINT",EDGE,{"derivedFrom":subQ1}),1.0]])]});}
            var Q1;
            Q1=makeQuery(id+"F16.imprint","IMPRINT",FACE,{"disambiguationData":[TD([[makeQuery(id+"F16.imprint","IMPRINT",EDGE,{"derivedFrom":sQuery(id+"F16.wireOp",EDGE,"E23")}),-1.0]])]});
            var Q2;
            {var subQ0=sQuery(id+"F16.wireOp",EDGE,"E24");var subQ1=sQuery(id+"F16.wireOp",EDGE,"E22");var subQ2=makeQuery(id+"F16.imprint","INTERSECT",VERTEX,{"derivedFrom":[subQ1,subQ0]});Q2=makeQuery(id+"F16.imprint","IMPRINT",FACE,{"disambiguationData":[TD([[makeQuery(id+"F16.imprint","IMPRINT",EDGE,{"disambiguationData":[TD([[subQ2,-1.0]])],"derivedFrom":subQ1}),-1.0]])]});}
            var Q3;
            {var subQ0=sQuery(id+"F6.wireOp",EDGE,"E10");var subQ1=sQuery(id+"F6.wireOp",EDGE,"E6.right");var subQ2=sQuery(id+"F6.wireOp",EDGE,"E6.left");var subQ3=sQuery(id+"F0.wireOp",EDGE,"E0.right");var subQ4=makeQuery(id+"F7.boolean.opBoolean","MERGE",FACE,{"derivedFrom":[makeQuery(id+"F1.opExtrude","SWEPT_FACE",FACE,{"disambiguationData":[OSD([subQ3])]}),makeQuery(id+"F7.opExtrude","CAP_FACE",FACE,{"disambiguationData":[OSD([sQuery(id+"F6.wireOp",EDGE,"E6.bottom"),subQ2,subQ1,sQuery(id+"F6.wireOp",EDGE,"E7"),subQ0])],"isStart":true})]});var subQ5=makeQuery(id+"F11.opFillet","BLEND_EDGE",EDGE,{"blendedFrom":[makeQuery(id+"F7.opExtrude","CAP_EDGE",EDGE,{"disambiguationData":[OSD([subQ0])],"isStart":true}),subQ4],"blendedInto":[subQ4]});Q3=makeQuery(id+"F16.imprint","IMPRINT",FACE,{"disambiguationData":[TD([[makeQuery(id+"F16.imprint","IMPRINT",EDGE,{"derivedFrom":subQ5}),-1.0]])]});}
            extrude(context, id + "F17", {"entities" : qUnion([Q0, Q1, Q2, Q3]), "depth" : 5 * mm});
        }
        {
            var Q0;
            Q0=makeQuery(id+"F17.opExtrude","SWEPT_FACE",FACE,{"disambiguationData":[OSD([sQuery(id+"F16.wireOp",EDGE,"E25")])]});
            var sketch = newSketch(context, id + "F18", { "sketchPlane" : qUnion([Q0])});
            skCircle(sketch, "E27", {"center": v(35.5, -5) * mm, "radius": 5 * mm});
            skPoint(sketch, "E28", {"position": v(15.5, -5) * mm});
            skLineSegment(sketch, "E29", {"start": v(20.5, 0) * mm, "end": v(35.5, 0) * mm});
            skLineSegment(sketch, "E30", {"start": v(35.5, -10) * mm, "end": v(20.5, -10) * mm});
            skCircle(sketch, "E31", {"center": v(35.5, -5) * mm, "radius": 2.75 * mm});
            skSolve(sketch);
        }
        {
            var Q0;
            {var subQ0=sQuery(id+"F16.wireOp",EDGE,"E25");Q0=makeQuery(id+"F18.imprint","IMPRINT",FACE,{"disambiguationData":[TD([[makeQuery(id+"F18.imprint","IMPRINT",EDGE,{"derivedFrom":makeQuery(id+"F17.opExtrude","CAP_EDGE",EDGE,{"disambiguationData":[OSD([subQ0])],"isStart":true})}),1.0]])]});}
            var Q1;
            {var subQ0=sQuery(id+"F18.wireOp",EDGE,"E29");Q1=makeQuery(id+"F18.imprint","IMPRINT",FACE,{"disambiguationData":[TD([[makeQuery(id+"F18.imprint","IMPRINT",EDGE,{"derivedFrom":subQ0}),-1.0]])]});}
            var Q2;
            Q2=makeQuery(id+"F18.imprint","IMPRINT",FACE,{"disambiguationData":[TD([[makeQuery(id+"F18.imprint","IMPRINT",EDGE,{"derivedFrom":sQuery(id+"F18.wireOp",EDGE,"E31")}),-1.0]])]});
            var Q3;
            {var subQ0=sQuery(id+"F18.wireOp",EDGE,"E30");Q3=makeQuery(id+"F18.imprint","IMPRINT",FACE,{"disambiguationData":[TD([[makeQuery(id+"F18.imprint","IMPRINT",EDGE,{"derivedFrom":subQ0}),-1.0]])]});}
            extrude(context, id + "F19", {"entities" : qUnion([Q0, Q1, Q2, Q3]), "operationType" : NewBodyOperationType.ADD, "depth" : 5 * mm});
        }
        {
            var Q0;
            Q0=makeQuery(id+"F19.opExtrude","CAP_FACE",FACE,{"disambiguationData":[OSD([sQuery(id+"F16.wireOp",EDGE,"E24"),sQuery(id+"F16.wireOp",EDGE,"E25"),sQuery(id+"F16.wireOp",EDGE,"E26"),sQuery(id+"F18.wireOp",EDGE,"E27"),sQuery(id+"F18.wireOp",EDGE,"E29"),sQuery(id+"F18.wireOp",EDGE,"E30"),sQuery(id+"F18.wireOp",EDGE,"E31")])],"isStart":true});
            var sketch = newSketch(context, id + "F20", { "sketchPlane" : qUnion([Q0])});
            skCircle(sketch, "E32.cCircle", {"center": v(-35.5, -5) * mm, "radius": 4 * mm, "construction": true});
            skLineSegment(sketch, "E32.0", {"start": v(-37.8, -1) * mm, "end": v(-33.2, -1) * mm});
            skLineSegment(sketch, "E32.1", {"start": v(-33.2, -1) * mm, "end": v(-30.88, -5) * mm});
            skLineSegment(sketch, "E32.2", {"start": v(-30.88, -5) * mm, "end": v(-33.2, -9) * mm});
            skLineSegment(sketch, "E32.3", {"start": v(-33.2, -9) * mm, "end": v(-37.8, -9) * mm});
            skLineSegment(sketch, "E32.4", {"start": v(-37.8, -9) * mm, "end": v(-40.12, -5) * mm});
            skLineSegment(sketch, "E32.5", {"start": v(-40.12, -5) * mm, "end": v(-37.8, -1) * mm});
            skPoint(sketch, "E32.0.midPoint", {"position": v(-35.5, -1) * mm});
            skCircle(sketch, "E33", {"center": v(-23.5, -5) * mm, "radius": 1.5 * mm});
            skCircle(sketch, "E34", {"center": v(-35.5, -5) * mm, "radius": 6.62 * mm});
            skLineSegment(sketch, "E35", {"start": v(-35.5, -5) * mm, "end": v(-30.82, -0.32) * mm});
            skLineSegment(sketch, "E36", {"start": v(-35.5, -5) * mm, "end": v(-30.82, -9.68) * mm});
            skArc(sketch, "E37", {"start": v(-23.45, -6.5) * mm, "mid": v(-27.44, -7.39) * mm, "end": v(-30.82, -9.68) * mm});
            skArc(sketch, "E38", {"start": v(-30.82, -0.32) * mm, "mid": v(-27.44, -2.61) * mm, "end": v(-23.45, -3.5) * mm});
            skArc(sketch, "E39.1.0", {"start": v(-34, 7.05) * mm, "mid": v(-33.11, 3.06) * mm, "end": v(-30.82, -0.32) * mm});
            skCircle(sketch, "E39.1.1", {"center": v(-35.5, 7) * mm, "radius": 1.5 * mm});
            skArc(sketch, "E39.1.2", {"start": v(-40.18, -0.32) * mm, "mid": v(-37.89, 3.06) * mm, "end": v(-37, 7.05) * mm});
            skArc(sketch, "E39.2.0", {"start": v(-47.55, -3.5) * mm, "mid": v(-43.56, -2.61) * mm, "end": v(-40.18, -0.32) * mm});
            skCircle(sketch, "E39.2.1", {"center": v(-47.5, -5) * mm, "radius": 1.5 * mm});
            skArc(sketch, "E39.2.2", {"start": v(-40.18, -9.68) * mm, "mid": v(-43.56, -7.39) * mm, "end": v(-47.55, -6.5) * mm});
            skArc(sketch, "E39.3.0", {"start": v(-37, -17.05) * mm, "mid": v(-37.89, -13.06) * mm, "end": v(-40.18, -9.68) * mm});
            skCircle(sketch, "E39.3.1", {"center": v(-35.5, -17) * mm, "radius": 1.5 * mm});
            skArc(sketch, "E39.3.2", {"start": v(-30.82, -9.68) * mm, "mid": v(-33.11, -13.06) * mm, "end": v(-34, -17.05) * mm});
            skSolve(sketch);
        }
        {
            var Q0;
            {var subQ6=makeQuery(id+"F19.opExtrude","CAP_EDGE",EDGE,{"disambiguationData":[OSD([sQuery(id+"F18.wireOp",EDGE,"E27")])],"isStart":true});Q0=makeQuery(id+"F20.imprint","IMPRINT",FACE,{"disambiguationData":[TD([[makeQuery(id+"F20.imprint","IMPRINT",EDGE,{"derivedFrom":subQ6}),1.0]])]});}
            var Q1;
            {var subQ15=sQuery(id+"F20.wireOp",EDGE,"E32.0");Q1=makeQuery(id+"F20.imprint","IMPRINT",FACE,{"disambiguationData":[TD([[makeQuery(id+"F20.imprint","IMPRINT",EDGE,{"derivedFrom":subQ15}),1.0]])]});}
            var Q2;
            {var subQ5=sQuery(id+"F20.wireOp",EDGE,"E32.2");var subQ6=sQuery(id+"F20.wireOp",EDGE,"E32.1");var subQ7=makeQuery(id+"F20.imprint","INTERSECT",VERTEX,{"derivedFrom":[subQ6,subQ5]});Q2=makeQuery(id+"F20.imprint","IMPRINT",FACE,{"disambiguationData":[TD([[makeQuery(id+"F20.imprint","IMPRINT",EDGE,{"disambiguationData":[TD([[subQ7,1.0]])],"derivedFrom":subQ6}),1.0]])]});}
            var Q3;
            {var subQ0=sQuery(id+"F20.wireOp",EDGE,"E37");Q3=makeQuery(id+"F20.imprint","IMPRINT",FACE,{"disambiguationData":[TD([[makeQuery(id+"F20.imprint","IMPRINT",EDGE,{"derivedFrom":subQ0}),-1.0]])]});}
            var Q4;
            {var subQ0=sQuery(id+"F20.wireOp",EDGE,"E33");var subQ1=makeQuery(id+"F20.imprint","INTERSECT",VERTEX,{"derivedFrom":[subQ0,sQuery(id+"F20.wireOp",EDGE,"E37")]});Q4=makeQuery(id+"F20.imprint","IMPRINT",FACE,{"disambiguationData":[TD([[makeQuery(id+"F20.imprint","IMPRINT",EDGE,{"disambiguationData":[TD([[subQ1,1.0]])],"derivedFrom":subQ0}),1.0]])]});}
            var Q5;
            {var subQ18=sQuery(id+"F20.wireOp",EDGE,"E39.1.2");Q5=makeQuery(id+"F20.imprint","IMPRINT",FACE,{"disambiguationData":[TD([[makeQuery(id+"F20.imprint","IMPRINT",EDGE,{"derivedFrom":subQ18}),-1.0]])]});}
            var Q6;
            {var subQ0=sQuery(id+"F20.wireOp",EDGE,"E39.2.1");var subQ1=makeQuery(id+"F20.imprint","INTERSECT",VERTEX,{"derivedFrom":[sQuery(id+"F20.wireOp",EDGE,"E39.2.0"),subQ0]});Q6=makeQuery(id+"F20.imprint","IMPRINT",FACE,{"disambiguationData":[TD([[makeQuery(id+"F20.imprint","IMPRINT",EDGE,{"disambiguationData":[TD([[subQ1,1.0]])],"derivedFrom":subQ0}),1.0]])]});}
            var Q7;
            {var subQ0=sQuery(id+"F20.wireOp",EDGE,"E39.3.1");var subQ1=makeQuery(id+"F20.imprint","INTERSECT",VERTEX,{"derivedFrom":[sQuery(id+"F20.wireOp",EDGE,"E39.3.0"),subQ0]});Q7=makeQuery(id+"F20.imprint","IMPRINT",FACE,{"disambiguationData":[TD([[makeQuery(id+"F20.imprint","IMPRINT",EDGE,{"disambiguationData":[TD([[subQ1,1.0]])],"derivedFrom":subQ0}),1.0]])]});}
            var Q8;
            {var subQ0=sQuery(id+"F20.wireOp",EDGE,"E39.1.1");var subQ1=makeQuery(id+"F20.imprint","INTERSECT",VERTEX,{"derivedFrom":[sQuery(id+"F20.wireOp",EDGE,"E39.1.0"),subQ0]});Q8=makeQuery(id+"F20.imprint","IMPRINT",FACE,{"disambiguationData":[TD([[makeQuery(id+"F20.imprint","IMPRINT",EDGE,{"disambiguationData":[TD([[subQ1,1.0]])],"derivedFrom":subQ0}),1.0]])]});}
            var Q9;
            {var subQ0=sQuery(id+"F20.wireOp",EDGE,"E39.1.0");var subQ1=sQuery(id+"F20.wireOp",EDGE,"E34");var subQ2=makeQuery(id+"F20.imprint","INTERSECT",VERTEX,{"derivedFrom":[subQ1,sQuery(id+"F20.wireOp",EDGE,"E35"),sQuery(id+"F20.wireOp",EDGE,"E38"),subQ0]});Q9=makeQuery(id+"F20.imprint","IMPRINT",FACE,{"disambiguationData":[TD([[makeQuery(id+"F20.imprint","IMPRINT",EDGE,{"disambiguationData":[TD([[subQ2,-1.0]])],"derivedFrom":subQ1}),-1.0]])]});}
            var Q10;
            {var subQ0=sQuery(id+"F20.wireOp",EDGE,"E39.3.2");var subQ1=sQuery(id+"F20.wireOp",EDGE,"E34");var subQ2=makeQuery(id+"F20.imprint","INTERSECT",VERTEX,{"derivedFrom":[subQ1,sQuery(id+"F20.wireOp",EDGE,"E36"),sQuery(id+"F20.wireOp",EDGE,"E37"),subQ0]});Q10=makeQuery(id+"F20.imprint","IMPRINT",FACE,{"disambiguationData":[TD([[makeQuery(id+"F20.imprint","IMPRINT",EDGE,{"disambiguationData":[TD([[subQ2,1.0]])],"derivedFrom":subQ1}),-1.0]])]});}
            extrude(context, id + "F21", {"entities" : qUnion([Q0, Q1, Q2, Q3, Q4, Q5, Q6, Q7, Q8, Q9, Q10]), "depth" : 10 * mm});
        }
        {
            var Q0;
            Q0=makeQuery(id+"F21.opExtrude","CAP_FACE",FACE,{"disambiguationData":[OSD([sQuery(id+"F16.wireOp",EDGE,"E24"),sQuery(id+"F16.wireOp",EDGE,"E25"),sQuery(id+"F16.wireOp",EDGE,"E26"),sQuery(id+"F18.wireOp",EDGE,"E29"),sQuery(id+"F18.wireOp",EDGE,"E30"),sQuery(id+"F20.wireOp",EDGE,"E32.0"),sQuery(id+"F20.wireOp",EDGE,"E32.1"),sQuery(id+"F20.wireOp",EDGE,"E32.2"),sQuery(id+"F20.wireOp",EDGE,"E32.3"),sQuery(id+"F20.wireOp",EDGE,"E32.4"),sQuery(id+"F20.wireOp",EDGE,"E32.5"),sQuery(id+"F20.wireOp",EDGE,"E33"),sQuery(id+"F20.wireOp",EDGE,"E34"),sQuery(id+"F20.wireOp",EDGE,"E37"),sQuery(id+"F20.wireOp",EDGE,"E38"),sQuery(id+"F20.wireOp",EDGE,"E39.1.0"),sQuery(id+"F20.wireOp",EDGE,"E39.1.1"),sQuery(id+"F20.wireOp",EDGE,"E39.1.2"),sQuery(id+"F20.wireOp",EDGE,"E39.2.0"),sQuery(id+"F20.wireOp",EDGE,"E39.2.1"),sQuery(id+"F20.wireOp",EDGE,"E39.2.2"),sQuery(id+"F20.wireOp",EDGE,"E39.3.0"),sQuery(id+"F20.wireOp",EDGE,"E39.3.1"),sQuery(id+"F20.wireOp",EDGE,"E39.3.2")])],"isStart":false});
            var sketch = newSketch(context, id + "F22", { "sketchPlane" : qUnion([Q0])});
            skSolve(sketch);
        }
        {
            var Q0;
            Q0=makeQuery(id+"F22.imprint","IMPRINT",FACE,{"disambiguationData":[TD([[makeQuery(id+"F22.imprint","IMPRINT",EDGE,{"derivedFrom":makeQuery(id+"F21.opExtrude","CAP_EDGE",EDGE,{"disambiguationData":[OSD([sQuery(id+"F20.wireOp",EDGE,"E32.0")])],"isStart":false})}),-1.0]])]});
            extrude(context, id + "F23", {"entities" : qUnion([Q0]), "operationType" : NewBodyOperationType.ADD, "oppositeDirection" : true, "depth" : 4 * mm});
        }
        {
            var Q0;
            Q0=makeQuery(id+"F19.opExtrude","CAP_FACE",FACE,{"disambiguationData":[OSD([sQuery(id+"F16.wireOp",EDGE,"E24"),sQuery(id+"F16.wireOp",EDGE,"E25"),sQuery(id+"F16.wireOp",EDGE,"E26"),sQuery(id+"F18.wireOp",EDGE,"E27"),sQuery(id+"F18.wireOp",EDGE,"E29"),sQuery(id+"F18.wireOp",EDGE,"E30"),sQuery(id+"F18.wireOp",EDGE,"E31")])],"isStart":false});
            var sketch = newSketch(context, id + "F24", { "sketchPlane" : qUnion([Q0])});
            skCircle(sketch, "E40", {"center": v(35.5, -5) * mm, "radius": 5 * mm});
            skCircle(sketch, "E41", {"center": v(35.5, -5) * mm, "radius": 2.75 * mm});
            skLineSegment(sketch, "E42", {"start": v(30.5, -5) * mm, "end": v(30.5, -23.5) * mm});
            skLineSegment(sketch, "E43", {"start": v(40.5, -5) * mm, "end": v(40.5, -23.5) * mm});
            skLineSegment(sketch, "E44.bottom", {"start": v(40.5, -23.5) * mm, "end": v(10.5, -23.5) * mm});
            skLineSegment(sketch, "E44.top", {"start": v(40.5, -28.5) * mm, "end": v(10.5, -28.5) * mm});
            skLineSegment(sketch, "E44.left", {"start": v(40.5, -23.5) * mm, "end": v(40.5, -28.5) * mm});
            skLineSegment(sketch, "E44.right", {"start": v(10.5, -23.5) * mm, "end": v(10.5, -28.5) * mm});
            skPoint(sketch, "E45", {"position": v(35.5, -34.01) * mm});
            skPoint(sketch, "E46", {"position": v(15.5, -23.5) * mm});
            skSolve(sketch);
        }
        {
            var Q0;
            {var subQ3=sQuery(id+"F24.wireOp",EDGE,"E43");Q0=makeQuery(id+"F24.imprint","IMPRINT",FACE,{"disambiguationData":[TD([[makeQuery(id+"F24.imprint","IMPRINT",EDGE,{"derivedFrom":subQ3}),-1.0]])]});}
            var Q1;
            Q1=makeQuery(id+"F24.imprint","IMPRINT",FACE,{"disambiguationData":[TD([[makeQuery(id+"F24.imprint","IMPRINT",EDGE,{"derivedFrom":sQuery(id+"F24.wireOp",EDGE,"E44.top")}),-1.0]])]});
            var Q2;
            Q2=makeQuery(id+"F24.imprint","IMPRINT",FACE,{"disambiguationData":[TD([[makeQuery(id+"F24.imprint","IMPRINT",EDGE,{"derivedFrom":sQuery(id+"F24.wireOp",EDGE,"E41")}),-1.0]])]});
            var Q3;
            {var subQ0=sQuery(id+"F24.wireOp",EDGE,"E40");var subQ3=sQuery(id+"F24.wireOp",EDGE,"E42");var subQ4=makeQuery(id+"F24.imprint","INTERSECT",VERTEX,{"derivedFrom":[subQ0,subQ3]});Q3=makeQuery(id+"F24.imprint","IMPRINT",FACE,{"disambiguationData":[TD([[makeQuery(id+"F24.imprint","IMPRINT",EDGE,{"disambiguationData":[TD([[subQ4,-1.0]])],"derivedFrom":subQ0}),-1.0]])]});}
            extrude(context, id + "F25", {"entities" : qUnion([Q0, Q1, Q2, Q3]), "depth" : 6 * mm});
        }
        {
            var Q0;
            Q0=makeQuery(id+"F25.opExtrude","CAP_FACE",FACE,{"disambiguationData":[OSD([sQuery(id+"F24.wireOp",EDGE,"E40"),sQuery(id+"F24.wireOp",EDGE,"E41"),sQuery(id+"F24.wireOp",EDGE,"E42"),sQuery(id+"F24.wireOp",EDGE,"E43"),sQuery(id+"F24.wireOp",EDGE,"E44.bottom"),sQuery(id+"F24.wireOp",EDGE,"E44.top"),sQuery(id+"F24.wireOp",EDGE,"E44.left"),sQuery(id+"F24.wireOp",EDGE,"E44.right")])],"isStart":true});
            var sketch = newSketch(context, id + "F26", { "sketchPlane" : qUnion([Q0])});
            skLineSegment(sketch, "E47.bottom", {"start": v(-10.5, -23.5) * mm, "end": v(-40.5, -23.5) * mm});
            skLineSegment(sketch, "E47.top", {"start": v(-10.5, -28.5) * mm, "end": v(-40.5, -28.5) * mm});
            skLineSegment(sketch, "E47.left", {"start": v(-10.5, -23.5) * mm, "end": v(-10.5, -28.5) * mm});
            skLineSegment(sketch, "E47.right", {"start": v(-40.5, -23.5) * mm, "end": v(-40.5, -28.5) * mm});
            skSolve(sketch);
        }
        {
            var Q0;
            Q0=qSketchRegion(id+"F26",true);
            extrude(context, id + "F27", {"entities" : qUnion([Q0]), "operationType" : NewBodyOperationType.ADD, "depth" : 25 * mm});
        }
        {
            var Q0;
            Q0=makeQuery(id+"F27.boolean.opBoolean","MERGE",FACE,{"derivedFrom":[makeQuery(id+"F25.opExtrude","SWEPT_FACE",FACE,{"disambiguationData":[OSD([sQuery(id+"F24.wireOp",EDGE,"E44.bottom")])]}),makeQuery(id+"F27.opExtrude","SWEPT_FACE",FACE,{"disambiguationData":[OSD([sQuery(id+"F26.wireOp",EDGE,"E47.bottom")])]})]});
            var sketch = newSketch(context, id + "F28", { "sketchPlane" : qUnion([Q0])});
            skPoint(sketch, "E48", {"position": v(15.5, -30) * mm});
            skPoint(sketch, "E49", {"position": v(35.5, -9) * mm});
            skSolve(sketch);
        }
        {
            var Q0;
            Q0=sQuery(id+"F28.wireOp",VERTEX,"E48");
            var Q1;
            Q1=sQuery(id+"F28.wireOp",VERTEX,"E49");
            var Q2;
            Q2=makeQuery(id+"F25.opExtrude","SWEPT_BODY",BODY,{"disambiguationData":[OSD([sQuery(id+"F24.wireOp",EDGE,"E40"),sQuery(id+"F24.wireOp",EDGE,"E41"),sQuery(id+"F24.wireOp",EDGE,"E42"),sQuery(id+"F24.wireOp",EDGE,"E43"),sQuery(id+"F24.wireOp",EDGE,"E44.bottom"),sQuery(id+"F24.wireOp",EDGE,"E44.top"),sQuery(id+"F24.wireOp",EDGE,"E44.left"),sQuery(id+"F24.wireOp",EDGE,"E44.right")])]});
            hole(context, id + "F29", {"style" : HoleStyle.SIMPLE, "endStyle" : HoleEndStyle.THROUGH, "standardTappedOrClearance" : lookupTablePath({ "standard" : "ISO", "fit" : "Normal", "size" : "M5", "type" : "Clearance" }), "standardBlindInLast" : lookupTablePath({ "fit" : "Standard", "standard" : "ISO", "size" : "M5", "type" : "Clearance" }), "holeDiameter" : 5.5 * mm, "tappedDepth" : 13.2 * mm, "tapClearance" : 3, "startFromSketch" : true, "locations" : qUnion([Q0, Q1]), "scope" : qUnion([Q2])});
        }
        {
            var Q0;
            Q0=makeQuery(id+"F27.boolean.opBoolean","MERGE",FACE,{"derivedFrom":[makeQuery(id+"F25.opExtrude","SWEPT_FACE",FACE,{"disambiguationData":[OSD([sQuery(id+"F24.wireOp",EDGE,"E44.top")])]}),makeQuery(id+"F27.opExtrude","SWEPT_FACE",FACE,{"disambiguationData":[OSD([sQuery(id+"F26.wireOp",EDGE,"E47.top")])]})]});
            var sketch = newSketch(context, id + "F30", { "sketchPlane" : qUnion([Q0])});
            skCircle(sketch, "E50", {"center": v(15.5, 30) * mm, "radius": 5 * mm});
            skCircle(sketch, "E51", {"center": v(35.5, 9) * mm, "radius": 5 * mm});
            skLineSegment(sketch, "E52", {"start": v(15.52, 25) * mm, "end": v(30.45, 25.05) * mm});
            skLineSegment(sketch, "E53", {"start": v(30.45, 25.05) * mm, "end": v(30.5, 8.98) * mm});
            skSolve(sketch);
        }
        {
            var Q0;
            {var subQ0=sQuery(id+"F30.wireOp",EDGE,"E50");var subQ1=sQuery(id+"F24.wireOp",EDGE,"E44.top");var subQ4=makeQuery(id+"F25.opExtrude","CAP_EDGE",EDGE,{"disambiguationData":[OSD([subQ1])],"isStart":false});var subQ5=makeQuery(id+"F30.imprint","INTERSECT",VERTEX,{"derivedFrom":[subQ4,subQ0]});Q0=makeQuery(id+"F30.imprint","IMPRINT",FACE,{"disambiguationData":[TD([[makeQuery(id+"F30.imprint","IMPRINT",EDGE,{"disambiguationData":[TD([[subQ5,-1.0]])],"derivedFrom":subQ0}),-1.0]])]});}
            var Q1;
            {var subQ7=sQuery(id+"F30.wireOp",EDGE,"E52");Q1=makeQuery(id+"F30.imprint","IMPRINT",FACE,{"disambiguationData":[TD([[makeQuery(id+"F30.imprint","IMPRINT",EDGE,{"derivedFrom":subQ7}),-1.0]])]});}
            var Q2;
            {var subQ0=sQuery(id+"F30.wireOp",EDGE,"E51");var subQ1=sQuery(id+"F26.wireOp",EDGE,"E47.top");var subQ4=makeQuery(id+"F27.opExtrude","CAP_EDGE",EDGE,{"disambiguationData":[OSD([subQ1])],"isStart":false});var subQ5=makeQuery(id+"F30.imprint","INTERSECT",VERTEX,{"derivedFrom":[subQ4,subQ0]});Q2=makeQuery(id+"F30.imprint","IMPRINT",FACE,{"disambiguationData":[TD([[makeQuery(id+"F30.imprint","IMPRINT",EDGE,{"disambiguationData":[TD([[subQ5,-1.0]])],"derivedFrom":subQ0}),-1.0]])]});}
            extrude(context, id + "F31", {"entities" : qUnion([Q0, Q1, Q2]), "operationType" : NewBodyOperationType.REMOVE, "endBound" : BoundingType.UP_TO_NEXT, "oppositeDirection" : true, "depth" : 25 * mm});
        }
        {
            var Q0;
            Q0=makeQuery(id+"F13.opExtrude","CAP_EDGE",EDGE,{"disambiguationData":[OSD([sQuery(id+"F12.wireOp",EDGE,"E18")])],"isStart":false});
            var Q1;
            Q1=makeQuery(id+"F13.opExtrude","CAP_EDGE",EDGE,{"disambiguationData":[OSD([sQuery(id+"F12.wireOp",EDGE,"E20.1.1")])],"isStart":false});
            var Q2;
            Q2=makeQuery(id+"F13.opExtrude","CAP_EDGE",EDGE,{"disambiguationData":[OSD([sQuery(id+"F12.wireOp",EDGE,"E20.2.1")])],"isStart":false});
            var Q3;
            Q3=makeQuery(id+"F13.opExtrude","CAP_EDGE",EDGE,{"disambiguationData":[OSD([sQuery(id+"F12.wireOp",EDGE,"E20.3.2")])],"isStart":false});
            var Q4;
            Q4=makeQuery(id+"F13.opExtrude","CAP_EDGE",EDGE,{"disambiguationData":[OSD([sQuery(id+"F12.wireOp",EDGE,"E20.2.2")])],"isStart":false});
            var Q5;
            Q5=makeQuery(id+"F13.opExtrude","CAP_EDGE",EDGE,{"disambiguationData":[OSD([sQuery(id+"F12.wireOp",EDGE,"E20.1.2")])],"isStart":false});
            var Q6;
            Q6=makeQuery(id+"F13.opExtrude","CAP_EDGE",EDGE,{"disambiguationData":[OSD([sQuery(id+"F12.wireOp",EDGE,"E20.1.2")])],"isStart":true});
            var Q7;
            Q7=makeQuery(id+"F13.opExtrude","CAP_EDGE",EDGE,{"disambiguationData":[OSD([sQuery(id+"F12.wireOp",EDGE,"E20.3.2")])],"isStart":true});
            var Q8;
            Q8=makeQuery(id+"F13.opExtrude","CAP_EDGE",EDGE,{"disambiguationData":[OSD([sQuery(id+"F12.wireOp",EDGE,"E20.2.2")])],"isStart":true});
            fillet(context, id + "F32", {"entities" : qUnion([Q0, Q1, Q2, Q3, Q4, Q5, Q6, Q7, Q8]), "radius" : 1 * mm, "tangentPropagation" : true, "allowEdgeOverflow" : false});
        }
        {
            var Q0;
            Q0=makeQuery(id+"F19.opExtrude","CAP_EDGE",EDGE,{"disambiguationData":[OSD([sQuery(id+"F16.wireOp",EDGE,"E24"),sQuery(id+"F16.wireOp",EDGE,"E25"),sQuery(id+"F18.wireOp",EDGE,"E29")])],"isStart":true});
            var Q1;
            Q1=makeQuery(id+"F17.opExtrude","CAP_EDGE",EDGE,{"disambiguationData":[OSD([sQuery(id+"F16.wireOp",EDGE,"E24")])],"isStart":false});
            var Q2;
            {var subQ0=sQuery(id+"F16.wireOp",EDGE,"E24");Q2=makeQuery(id+"F19.boolean.opBoolean","MERGE",EDGE,{"derivedFrom":[makeQuery(id+"F17.opExtrude","CAP_EDGE",EDGE,{"disambiguationData":[OSD([subQ0])],"isStart":true}),makeQuery(id+"F19.opExtrude","SWEPT_EDGE",EDGE,{"disambiguationData":[OSD([subQ0,sQuery(id+"F16.wireOp",EDGE,"E25")])]})]});}
            var Q3;
            Q3=makeQuery(id+"F19.opExtrude","CAP_EDGE",EDGE,{"disambiguationData":[OSD([sQuery(id+"F16.wireOp",EDGE,"E25")])],"isStart":false});
            var Q4;
            Q4=makeQuery(id+"F19.opExtrude","CAP_EDGE",EDGE,{"disambiguationData":[OSD([sQuery(id+"F16.wireOp",EDGE,"E24"),sQuery(id+"F16.wireOp",EDGE,"E25"),sQuery(id+"F18.wireOp",EDGE,"E29")])],"isStart":false});
            fillet(context, id + "F33", {"entities" : qUnion([Q0, Q1, Q2, Q3, Q4]), "radius" : 1 * mm, "tangentPropagation" : true, "allowEdgeOverflow" : false});
        }
        {
            var Q0;
            Q0=makeQuery(id+"F21.opExtrude","CAP_EDGE",EDGE,{"disambiguationData":[OSD([sQuery(id+"F20.wireOp",EDGE,"E33")])],"isStart":false});
            var Q1;
            Q1=makeQuery(id+"F21.opExtrude","CAP_EDGE",EDGE,{"disambiguationData":[OSD([sQuery(id+"F20.wireOp",EDGE,"E39.2.1")])],"isStart":true});
            fillet(context, id + "F34", {"entities" : qUnion([Q0, Q1]), "radius" : 1 * mm, "tangentPropagation" : true, "allowEdgeOverflow" : false});
        }
        {
            var Q0;
            Q0=makeQuery(id+"F25.opExtrude","CAP_EDGE",EDGE,{"disambiguationData":[OSD([sQuery(id+"F24.wireOp",EDGE,"E40")])],"isStart":false});
            var Q1;
            {var subQ0=sQuery(id+"F30.wireOp",EDGE,"E50");var subQ1=sQuery(id+"F24.wireOp",EDGE,"E44.top");var subQ3=makeQuery(id+"F27.boolean.opBoolean","MERGE",FACE,{"derivedFrom":[makeQuery(id+"F25.opExtrude","SWEPT_FACE",FACE,{"disambiguationData":[OSD([sQuery(id+"F24.wireOp",EDGE,"E44.bottom")])]}),makeQuery(id+"F27.opExtrude","SWEPT_FACE",FACE,{"disambiguationData":[OSD([sQuery(id+"F26.wireOp",EDGE,"E47.bottom")])]})]});Q1=makeQuery(id+"F31.boolean.opBoolean","TWEAK_EDGE",EDGE,{"derivedFrom":[makeQuery(id+"F31.opExtrude","TWEAK_EDGE",EDGE,{"derivedFrom":[subQ3,makeQuery(id+"F30.imprint","IMPRINT",EDGE,{"disambiguationData":[TD([[makeQuery(id+"F30.imprint","INTERSECT",VERTEX,{"derivedFrom":[makeQuery(id+"F25.opExtrude","CAP_EDGE",EDGE,{"disambiguationData":[OSD([subQ1])],"isStart":false}),subQ0]}),-1.0]])],"derivedFrom":subQ0})]}),makeQuery(id+"F31.opExtrude","TWEAK_EDGE",EDGE,{"derivedFrom":[subQ3,makeQuery(id+"F30.imprint","IMPRINT",EDGE,{"disambiguationData":[TD([[makeQuery(id+"F30.imprint","INTERSECT",VERTEX,{"derivedFrom":[subQ0,sQuery(id+"F30.wireOp",EDGE,"E52")]}),1.0]])],"derivedFrom":subQ0})]})]});}
            var Q2;
            Q2=makeQuery(id+"F25.opExtrude","CAP_EDGE",EDGE,{"disambiguationData":[OSD([sQuery(id+"F24.wireOp",EDGE,"E40")])],"isStart":true});
            var Q3;
            {var subQ0=sQuery(id+"F30.wireOp",EDGE,"E50");var subQ1=sQuery(id+"F24.wireOp",EDGE,"E44.top");Q3=makeQuery(id+"F31.boolean.opBoolean","TWEAK_EDGE",EDGE,{"derivedFrom":[makeQuery(id+"F31.opExtrude","CAP_EDGE",EDGE,{"disambiguationData":[OSD([subQ0]),TDD([makeQuery(id+"F30.imprint","IMPRINT",EDGE,{"disambiguationData":[TD([[makeQuery(id+"F30.imprint","INTERSECT",VERTEX,{"derivedFrom":[makeQuery(id+"F25.opExtrude","CAP_EDGE",EDGE,{"disambiguationData":[OSD([subQ1])],"isStart":false}),subQ0]}),-1.0]])],"derivedFrom":subQ0})])],"isStart":true}),makeQuery(id+"F31.opExtrude","CAP_EDGE",EDGE,{"disambiguationData":[OSD([subQ0]),TDD([makeQuery(id+"F30.imprint","IMPRINT",EDGE,{"disambiguationData":[TD([[makeQuery(id+"F30.imprint","INTERSECT",VERTEX,{"derivedFrom":[subQ0,sQuery(id+"F30.wireOp",EDGE,"E52")]}),1.0]])],"derivedFrom":subQ0})])],"isStart":true})]});}
            var Q4;
            {var subQ0=sQuery(id+"F30.wireOp",EDGE,"E51");var subQ1=sQuery(id+"F26.wireOp",EDGE,"E47.top");var subQ2=makeQuery(id+"F30.imprint","INTERSECT",VERTEX,{"derivedFrom":[makeQuery(id+"F27.opExtrude","CAP_EDGE",EDGE,{"disambiguationData":[OSD([subQ1])],"isStart":false}),subQ0]});Q4=makeQuery(id+"F31.boolean.opBoolean","TWEAK_EDGE",EDGE,{"derivedFrom":[makeQuery(id+"F31.opExtrude","CAP_EDGE",EDGE,{"disambiguationData":[OSD([subQ0]),TDD([makeQuery(id+"F30.imprint","IMPRINT",EDGE,{"disambiguationData":[TD([[makeQuery(id+"F30.imprint","INTERSECT",VERTEX,{"derivedFrom":[subQ0,sQuery(id+"F30.wireOp",EDGE,"E53")]}),-1.0]])],"derivedFrom":subQ0})])],"isStart":true}),makeQuery(id+"F31.opExtrude","CAP_EDGE",EDGE,{"disambiguationData":[OSD([subQ0]),TDD([makeQuery(id+"F30.imprint","IMPRINT",EDGE,{"disambiguationData":[TD([[subQ2,-1.0]])],"derivedFrom":subQ0})])],"isStart":true})]});}
            var Q5;
            {var subQ0=sQuery(id+"F30.wireOp",EDGE,"E51");var subQ1=sQuery(id+"F26.wireOp",EDGE,"E47.top");var subQ2=makeQuery(id+"F30.imprint","INTERSECT",VERTEX,{"derivedFrom":[makeQuery(id+"F27.opExtrude","CAP_EDGE",EDGE,{"disambiguationData":[OSD([subQ1])],"isStart":false}),subQ0]});var subQ3=makeQuery(id+"F27.boolean.opBoolean","MERGE",FACE,{"derivedFrom":[makeQuery(id+"F25.opExtrude","SWEPT_FACE",FACE,{"disambiguationData":[OSD([sQuery(id+"F24.wireOp",EDGE,"E44.bottom")])]}),makeQuery(id+"F27.opExtrude","SWEPT_FACE",FACE,{"disambiguationData":[OSD([sQuery(id+"F26.wireOp",EDGE,"E47.bottom")])]})]});Q5=makeQuery(id+"F31.boolean.opBoolean","TWEAK_EDGE",EDGE,{"derivedFrom":[makeQuery(id+"F31.opExtrude","TWEAK_EDGE",EDGE,{"derivedFrom":[subQ3,makeQuery(id+"F30.imprint","IMPRINT",EDGE,{"disambiguationData":[TD([[makeQuery(id+"F30.imprint","INTERSECT",VERTEX,{"derivedFrom":[subQ0,sQuery(id+"F30.wireOp",EDGE,"E53")]}),-1.0]])],"derivedFrom":subQ0})]}),makeQuery(id+"F31.opExtrude","TWEAK_EDGE",EDGE,{"derivedFrom":[subQ3,makeQuery(id+"F30.imprint","IMPRINT",EDGE,{"disambiguationData":[TD([[subQ2,-1.0]])],"derivedFrom":subQ0})]})]});}
            var Q6;
            Q6=makeQuery(id+"F27.opExtrude","CAP_EDGE",EDGE,{"disambiguationData":[OSD([sQuery(id+"F26.wireOp",EDGE,"E47.bottom")])],"isStart":true});
            fillet(context, id + "F35", {"entities" : qUnion([Q0, Q1, Q2, Q3, Q4, Q5, Q6]), "radius" : 1 * mm, "tangentPropagation" : true, "allowEdgeOverflow" : false});
        }
    });
